# Revit family: 20L
name_source: partatom
category: Lighting Fixtures
revit_build: Autodesk Revit 2014 (Build: 20130308_1515(x64)
units: mm (PartAtom-declared; Revit-internal decimal feet)

## types (5) — shared parameters
Apparent Load = 9 VA
Assembly Code = D5020200
Color Filter = 16777215
Default Elevation = 48"
Description = Wall/Slot® 2000 LED
Dimming Lamp Color Temperature Shift = Incandescent Lamp Curve
Emit Shape Visible in Rendering = No
Emit from Rectangle Length = 3"
Finish = Hubbell - Arctic White
Glass = Hubbell - White Glass
Lamp = LED
Load Classification = Lighting
Manufacturer = Columbia Lighting
Model = 2000LED
Mounting Type = Perimeter
Photometric Link = https://www.hubbell.com
Photometric Notes = More IES files download in Photometric Web Link
Photometric Web File = 20L-Cx-35K-D060-04.ies
Power Factor = 1
Product Documentation Link = https://hubbellcdn.com
Product Page URL = https://www.hubbell.com
Tilt Angle = 90.00°
Type Comments = Lighting Fixture
URL = https://www.hubbell.com
Voltage = 120 V
Warranty = Five year warranty
Wattage Comments = 3.5W to 12.6
Watts = 9 W

## per-type parameters (varying)
| type | Emit from Rectangle Width | zz Length 2 |
| 20L-04 | 46" | 48" |
| 20L-02 | 22" | 24" |
| 20L-03 | 34" | 36" |
| 20L-06 | 70" | 72" |
| 20L-08 | 94" | 96" |

## geometry (parser evidence)
native form markers: Blend x2, Sweep x2
no freeform markers — native parametric forms only
